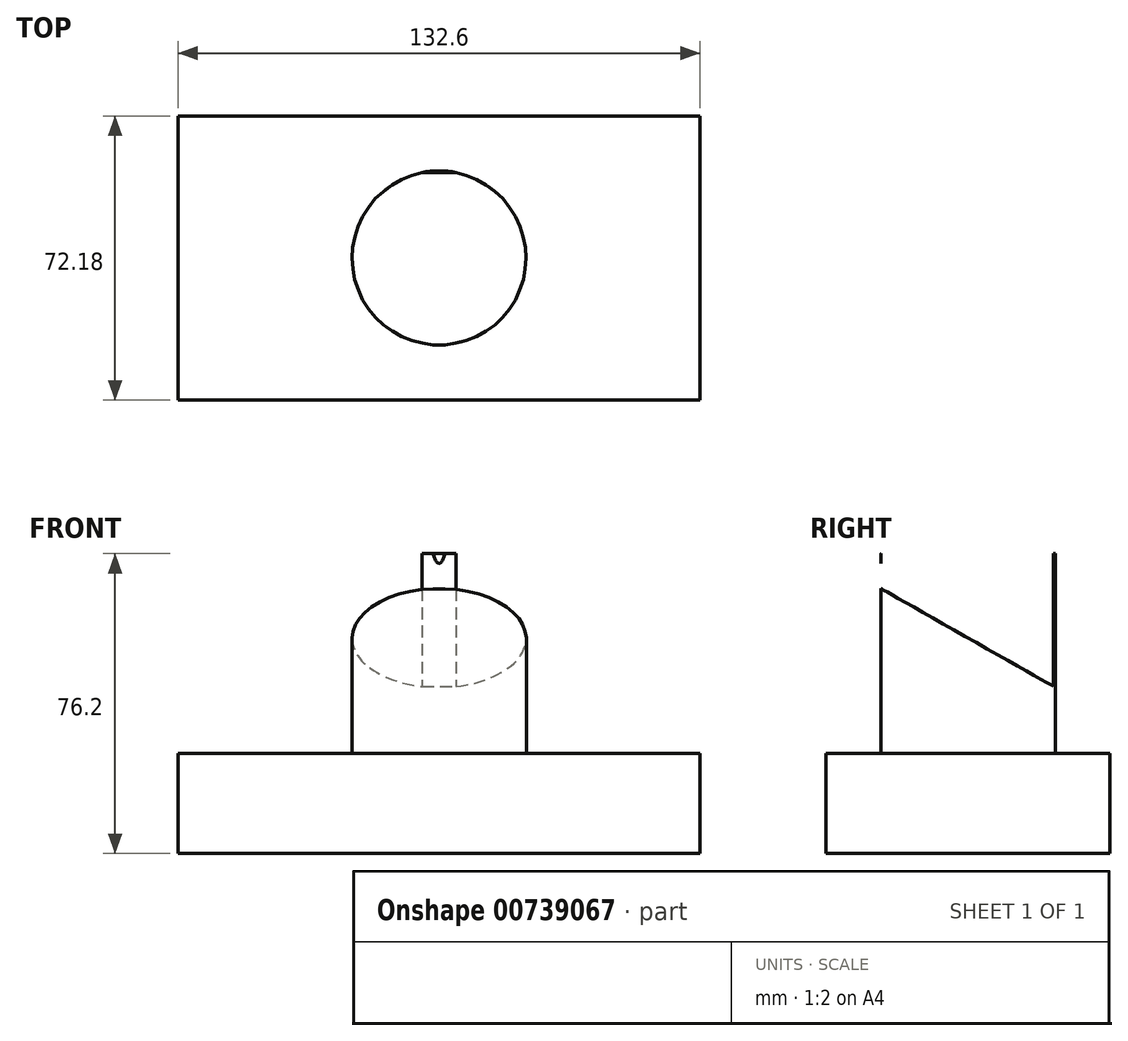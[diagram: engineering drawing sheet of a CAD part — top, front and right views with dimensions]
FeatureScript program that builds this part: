
annotation { "Feature Type Name" : "Feature", "Feature Type Description" : "" }
export const myFeature = defineFeature(function(context is Context, id is Id, definition is map)
    precondition{}
    {
        {
            var Q0;
            Q0=qCreatedBy(makeId("Top.planeOp"),FACE);
            var sketch = newSketch(context, id + "F0", { "sketchPlane" : qUnion([Q0])});
            skLineSegment(sketch, "E0.bottom", {"start": v(66.3, 36.09) * mm, "end": v(-66.3, 36.09) * mm});
            skLineSegment(sketch, "E0.top", {"start": v(66.3, -36.09) * mm, "end": v(-66.3, -36.09) * mm});
            skLineSegment(sketch, "E0.left", {"start": v(66.3, 36.09) * mm, "end": v(66.3, -36.09) * mm});
            skLineSegment(sketch, "E0.right", {"start": v(-66.3, 36.09) * mm, "end": v(-66.3, -36.09) * mm});
            skPoint(sketch, "E0.middle", {"position": v(0, 0) * mm});
            skSolve(sketch);
        }
        {
            var Q0;
            Q0=makeQuery(id+"F0.imprint","IMPRINT",FACE,{"disambiguationData":[TD([[makeQuery(id+"F0.imprint","IMPRINT",EDGE,{"derivedFrom":sQuery(id+"F0.wireOp",EDGE,"E0.bottom")}),1.0]])]});
            extrude(context, id + "F1", {"entities" : qUnion([Q0]), "depth" : 25.4 * mm, "offsetDistance" : 25.4 * mm});
        }
        {
            var Q0;
            Q0=makeQuery(id+"F1.opExtrude","CAP_FACE",FACE,{"disambiguationData":[OSD([sQuery(id+"F0.wireOp",EDGE,"E0.bottom"),sQuery(id+"F0.wireOp",EDGE,"E0.top"),sQuery(id+"F0.wireOp",EDGE,"E0.left"),sQuery(id+"F0.wireOp",EDGE,"E0.right")])],"isStart":false});
            var sketch = newSketch(context, id + "F2", { "sketchPlane" : qUnion([Q0])});
            skCircle(sketch, "E1", {"center": v(0, 0) * mm, "radius": 22.16 * mm});
            skSolve(sketch);
        }
        {
            var Q0;
            Q0=makeQuery(id+"F2.imprint","IMPRINT",FACE,{"disambiguationData":[TD([[makeQuery(id+"F2.imprint","IMPRINT",EDGE,{"derivedFrom":sQuery(id+"F2.wireOp",EDGE,"E1")}),1.0]])]});
            extrude(context, id + "F3", {"entities" : qUnion([Q0]), "operationType" : NewBodyOperationType.ADD, "depth" : 50.8 * mm, "offsetDistance" : 25.4 * mm});
        }
        {
            var Q0;
            Q0=qCreatedBy(makeId("Right.planeOp"),FACE);
            var sketch = newSketch(context, id + "F4", { "sketchPlane" : qUnion([Q0])});
            skLineSegment(sketch, "E2", {"start": v(-22.29, 67.42) * mm, "end": v(21.73, 42.43) * mm});
            skLineSegment(sketch, "E3", {"start": v(21.73, 42.43) * mm, "end": v(21.73, 76.37) * mm});
            skLineSegment(sketch, "E4", {"start": v(21.73, 76.37) * mm, "end": v(-22.1, 76.37) * mm});
            skLineSegment(sketch, "E5", {"start": v(-22.1, 76.37) * mm, "end": v(-22.29, 67.42) * mm});
            skSolve(sketch);
        }
        {
            var Q0;
            Q0=makeQuery(id+"F4.imprint","IMPRINT",FACE,{"disambiguationData":[TD([[makeQuery(id+"F4.imprint","IMPRINT",EDGE,{"derivedFrom":sQuery(id+"F4.wireOp",EDGE,"E2")}),1.0]])]});
            extrude(context, id + "F5", {"entities" : qUnion([Q0]), "operationType" : NewBodyOperationType.REMOVE, "oppositeDirection" : true, "depth" : 25.4 * mm, "offsetDistance" : 25.4 * mm, "hasSecondDirection" : true, "secondDirectionOppositeDirection" : false, "secondDirectionDepth" : 25.4 * mm});
        }
    });
